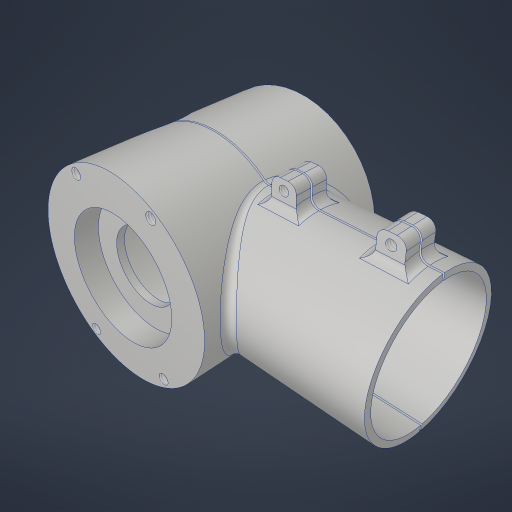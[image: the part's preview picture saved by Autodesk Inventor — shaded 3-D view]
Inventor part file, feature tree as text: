
AUTODESK INVENTOR PART (.ipt)
format: ipt  version: 2023.4 (Build 274418000, 418)  size: 893,440 bytes
history: native  units: in
note: dims shown in document units (in); Inventor stores cm internally (conversion verified against a paired STEP export)
features: sketch x17, extrude x11, projected_geometry x8, plane x7, hole x5, fillet x3, split x1
ambient origin geometry x8: Origin, YZ Plane, XZ Plane, XY Plane, X Axis, Y Axis, Z Axis, Center Point
bodies: Solid1 (feature_tree), Solid2 (feature_tree), Solid3 (feature_tree)
feature tree (52):
  extrude  "Extrusion1"  Depth=3.0in TaperAngle=0.0deg
  plane  "Work Plane1"
  extrude  "Extrusion2"  Depth=2.06in
  extrude  "Extrusion3"  Depth=3.0in TaperAngle=0.0deg
  hole  "Hole1"  [1 undecoded]
  plane  "Work Plane2"
  plane  "Work Plane3"
  extrude  "Extrusion5"  Depth=0.5in
  hole  "Hole2"  [1 undecoded]
  extrude  "Extrusion6"  Depth=1.375in
  hole  "Hole3"  [1 undecoded]
  fillet  "Fillet4"  [1 undecoded]
  hole  "Hole5"  [1 undecoded]
  sketch  "Sketch14"  dims[d45=2.375in]
  plane  "Work Plane4"
  extrude  "Extrusion8"  Depth=1.5in
  fillet  "Fillet5"  Radius=0.375in
  plane  "Work Plane5"
  extrude  "Extrusion9"  Depth=1.5in
  plane  "Work Plane6"
  extrude  "Extrusion10"  [1 undecoded]
  fillet  "Fillet6"  Radius=0.375in
  hole  "Hole6"  [1 undecoded]
  plane  "Work Plane7"
  extrude  "Extrusion11"  Depth=0.13in TaperAngle=0.0deg
  split  "Split1"
  extrude  "Extrusion12"  Depth=1.5in
  extrude  "Extrusion13"  Depth=1.5in
  sketch  "Sketch1"  dims[d0=3.0in d1=3.0in d2=0.0in]
  sketch  "Sketch2"  dims[d3=3.5in d4=2.06in]
  sketch  "Sketch3"  dims[d5=0.1in d6=3.0in d7=0.0in]
  sketch  "Sketch4"  dims[d8=3.3in d9=0.0in]
  sketch  "Sketch7"  dims[d11=1.125in d12=0.75in d13=1.875in d14=0.375in d15=0.5635in d16=1.625in d17=0.8108in d22=1.5in d27=-1.875in]
  sketch  "Sketch8"  dims[d28=0.375in d29=0.5in]
  sketch  "Sketch9"  dims[d30=1.0in d31=0.0in]
  sketch  "Sketch10"  dims[d34=1.125in d35=0.75in d36=1.875in d37=0.375in d38=0.5635in d39=1.0in d40=0.8108in d41=2.0in d42=0.0in]
  sketch  "Sketch13"  dims[d43=2.744in d44=1.375in]
  sketch  "Sketch15"  dims[d46=0.171in d47=0.432in d48=0.385in d49=0.25in d50=0.5635in d51=1.0in d52=0.8108in d69=0.13in]
  sketch  "Sketch16"  dims[d70=0.156in d71=0.38in d72=0.375in d73=0.25in d74=0.5635in d75=1.0in d76=0.8108in d77=45.0deg]
  sketch  "Sketch17"  dims[d78=1.0in d79=1.0in d80=0.0in]
  sketch  "Sketch18"  dims[d81=0.02in d83=1.5in d84=0.375in]
  sketch  "Sketch19"  dims[d85=0.5in d86=1.5in]
  sketch  "Sketch20"  dims[d87=0.5in d88=0.0in d89=-1.5in d90=0.375in]
  sketch  "Sketch21"  dims[d91=0.5in d92=1.5in d93=0.5in d94=0.0in d95=1.5in d96=1.5in d97=0.13in d98=0.145in d99=0.38in d100=0.385in d101=0.25in d102=0.5635in d103=1.0in d104=0.8108in d105=-2.0in d106=0.1in d107=0.125in d108=0.0in d109=0.015in d110=0.0in d111=0.015in d112=0.0in]
  projected_geometry  "Project Cut Edges3"
  projected_geometry  "Project Cut Edges4"
  projected_geometry  "Project Cut Edges5"
  projected_geometry  "Project Cut Edges6"
  projected_geometry  "Project Cut Edges7"
  projected_geometry  "Project Cut Edges8"
  projected_geometry  "Project Cut Edges9"
  projected_geometry  "Project Cut Edges10"
note: 7 required parameter values undecoded (feature->parameter linkage not recoverable at this tier; creation-order binding heuristic only, values carry confidence <= 0.55)
